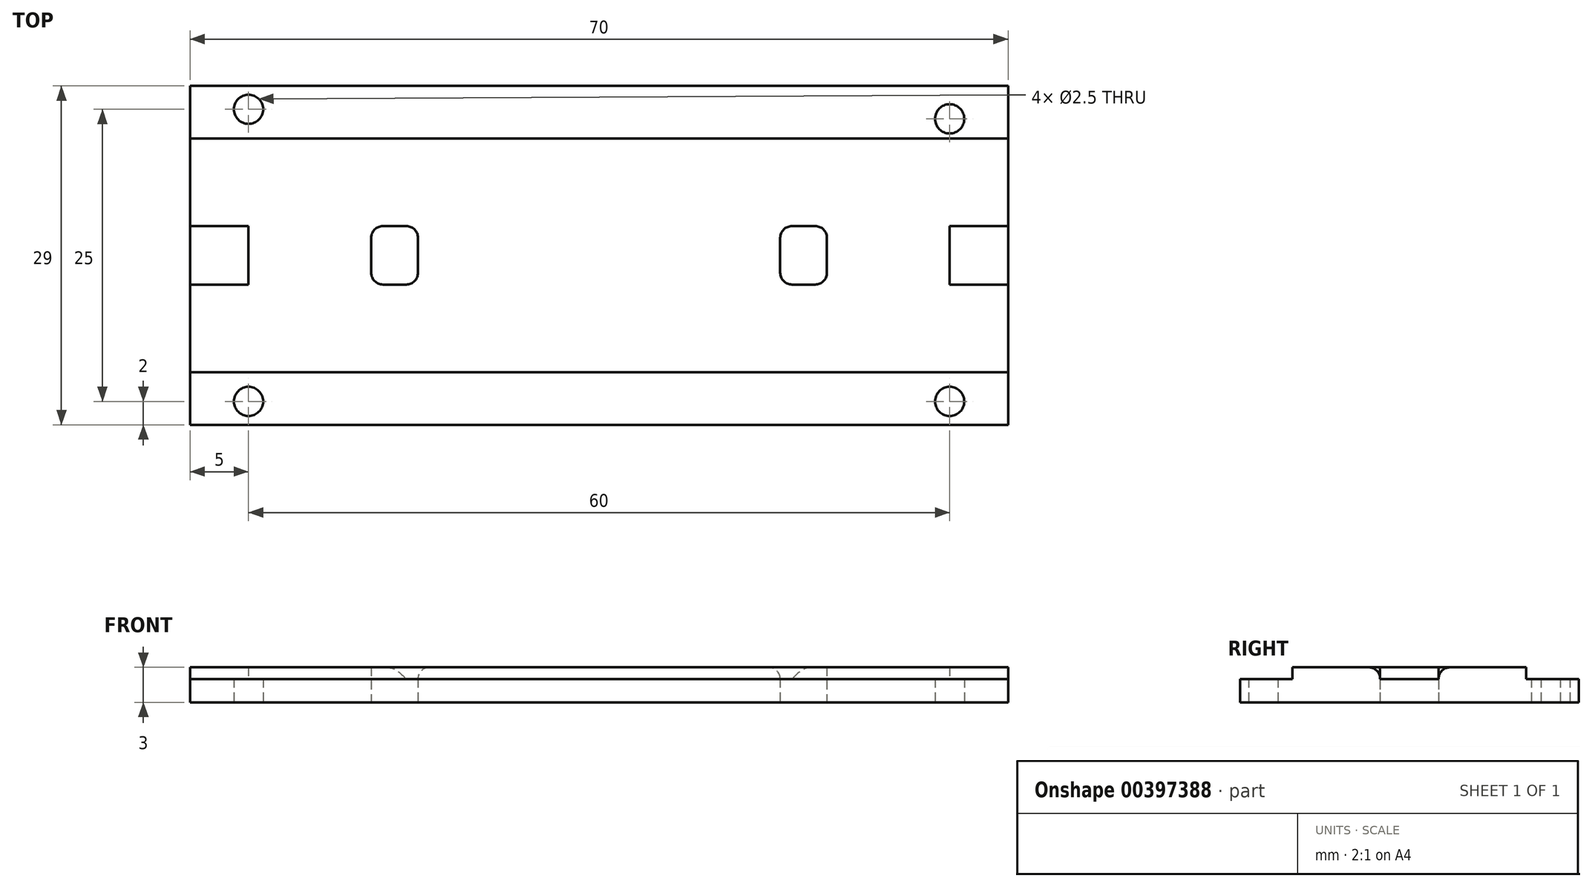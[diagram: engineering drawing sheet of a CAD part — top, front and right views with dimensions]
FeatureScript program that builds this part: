
annotation { "Feature Type Name" : "Feature", "Feature Type Description" : "" }
export const myFeature = defineFeature(function(context is Context, id is Id, definition is map)
    precondition{}
    {
        {
            var Q0;
            Q0=qCreatedBy(makeId("Top.planeOp"),FACE);
            var sketch = newSketch(context, id + "F0", { "sketchPlane" : qUnion([Q0])});
            skLineSegment(sketch, "E0.bottom", {"start": v(35, -14.5) * mm, "end": v(-35, -14.5) * mm});
            skLineSegment(sketch, "E0.top", {"start": v(35, 14.5) * mm, "end": v(-35, 14.5) * mm});
            skLineSegment(sketch, "E0.left", {"start": v(35, -14.5) * mm, "end": v(35, 14.5) * mm});
            skLineSegment(sketch, "E0.right", {"start": v(-35, -14.5) * mm, "end": v(-35, 14.5) * mm});
            skPoint(sketch, "E0.middle", {"position": v(0, 0) * mm});
            skLineSegment(sketch, "E1", {"start": v(-35, 10) * mm, "end": v(35, 10) * mm});
            skLineSegment(sketch, "E2", {"start": v(-35, -10) * mm, "end": v(35, -10) * mm});
            skLineSegment(sketch, "E3.bottom", {"start": v(-35, -2.5) * mm, "end": v(-30, -2.5) * mm});
            skLineSegment(sketch, "E3.top", {"start": v(-35, 2.5) * mm, "end": v(-30, 2.5) * mm});
            skLineSegment(sketch, "E3.left", {"start": v(-35, -2.5) * mm, "end": v(-35, 2.5) * mm});
            skLineSegment(sketch, "E3.right", {"start": v(-30, -2.5) * mm, "end": v(-30, 2.5) * mm});
            skPoint(sketch, "E3.middle", {"position": v(-32.5, 0) * mm});
            skPoint(sketch, "E3.middle.positionSnap0", {"position": v(-35, 0) * mm});
            skPoint(sketch, "E3.centerSnap0", {"position": v(-35, 0) * mm});
            skLineSegment(sketch, "E4.bottom", {"start": v(35, -2.5) * mm, "end": v(30, -2.5) * mm});
            skLineSegment(sketch, "E4.top", {"start": v(35, 2.5) * mm, "end": v(30, 2.5) * mm});
            skLineSegment(sketch, "E4.left", {"start": v(35, -2.5) * mm, "end": v(35, 2.5) * mm});
            skLineSegment(sketch, "E4.right", {"start": v(30, -2.5) * mm, "end": v(30, 2.5) * mm});
            skPoint(sketch, "E4.middle", {"position": v(32.5, 0) * mm});
            skPoint(sketch, "E4.cornerSnap0", {"position": v(-32.5, -2.5) * mm});
            skPoint(sketch, "E5", {"position": v(-30, -12.5) * mm});
            skPoint(sketch, "E6", {"position": v(30, -12.5) * mm});
            skPoint(sketch, "E7", {"position": v(30, 11.68) * mm});
            skPoint(sketch, "E8", {"position": v(-30, 12.5) * mm});
            skLineSegment(sketch, "E9.bottom", {"start": v(-15.5, -2.5) * mm, "end": v(-19.5, -2.5) * mm});
            skLineSegment(sketch, "E9.top", {"start": v(-15.5, 2.5) * mm, "end": v(-19.5, 2.5) * mm});
            skLineSegment(sketch, "E9.left", {"start": v(-15.5, -2.5) * mm, "end": v(-15.5, 2.5) * mm});
            skLineSegment(sketch, "E9.right", {"start": v(-19.5, -2.5) * mm, "end": v(-19.5, 2.5) * mm});
            skPoint(sketch, "E9.middle", {"position": v(-17.5, 0) * mm});
            skLineSegment(sketch, "E10.bottom", {"start": v(19.5, -2.5) * mm, "end": v(15.5, -2.5) * mm});
            skLineSegment(sketch, "E10.top", {"start": v(19.5, 2.5) * mm, "end": v(15.5, 2.5) * mm});
            skLineSegment(sketch, "E10.left", {"start": v(19.5, -2.5) * mm, "end": v(19.5, 2.5) * mm});
            skLineSegment(sketch, "E10.right", {"start": v(15.5, -2.5) * mm, "end": v(15.5, 2.5) * mm});
            skPoint(sketch, "E10.middle", {"position": v(17.5, 0) * mm});
            skSolve(sketch);
        }
        {
            var Q0;
            {var subQ4=sQuery(id+"F0.wireOp",EDGE,"E1");Q0=makeQuery(id+"F0.imprint","IMPRINT",FACE,{"disambiguationData":[TD([[makeQuery(id+"F0.imprint","IMPRINT",EDGE,{"derivedFrom":subQ4}),-1.0]])]});}
            extrude(context, id + "F1", {"entities" : qUnion([Q0]), "depth" : 3 * mm});
        }
        {
            var Q0;
            Q0=makeQuery(id+"F0.imprint","IMPRINT",FACE,{"disambiguationData":[TD([[makeQuery(id+"F0.imprint","IMPRINT",EDGE,{"derivedFrom":sQuery(id+"F0.wireOp",EDGE,"E3.bottom")}),1.0]])]});
            var Q1;
            {var subQ0=sQuery(id+"F0.wireOp",EDGE,"E0.top");Q1=makeQuery(id+"F0.imprint","IMPRINT",FACE,{"disambiguationData":[TD([[makeQuery(id+"F0.imprint","IMPRINT",EDGE,{"derivedFrom":subQ0}),1.0]])]});}
            var Q2;
            {var subQ0=sQuery(id+"F0.wireOp",EDGE,"E0.bottom");Q2=makeQuery(id+"F0.imprint","IMPRINT",FACE,{"disambiguationData":[TD([[makeQuery(id+"F0.imprint","IMPRINT",EDGE,{"derivedFrom":subQ0}),-1.0]])]});}
            var Q3;
            Q3=makeQuery(id+"F0.imprint","IMPRINT",FACE,{"disambiguationData":[TD([[makeQuery(id+"F0.imprint","IMPRINT",EDGE,{"derivedFrom":sQuery(id+"F0.wireOp",EDGE,"E4.bottom")}),-1.0]])]});
            extrude(context, id + "F2", {"entities" : qUnion([Q0, Q1, Q2, Q3]), "operationType" : NewBodyOperationType.ADD, "depth" : 2 * mm});
        }
        {
            var Q0;
            Q0=sQuery(id+"F0.wireOp",VERTEX,"E5");
            var Q1;
            Q1=sQuery(id+"F0.wireOp",VERTEX,"E8");
            var Q2;
            Q2=sQuery(id+"F0.wireOp",VERTEX,"E7");
            var Q3;
            Q3=sQuery(id+"F0.wireOp",VERTEX,"E6");
            var Q4;
            Q4=makeQuery(id+"F1.opExtrude","SWEPT_BODY",BODY,{"disambiguationData":[OSD([sQuery(id+"F0.wireOp",EDGE,"E0.left"),sQuery(id+"F0.wireOp",EDGE,"E0.right"),sQuery(id+"F0.wireOp",EDGE,"E1"),sQuery(id+"F0.wireOp",EDGE,"E2"),sQuery(id+"F0.wireOp",EDGE,"E3.bottom"),sQuery(id+"F0.wireOp",EDGE,"E3.top"),sQuery(id+"F0.wireOp",EDGE,"E3.right"),sQuery(id+"F0.wireOp",EDGE,"E4.bottom"),sQuery(id+"F0.wireOp",EDGE,"E4.top"),sQuery(id+"F0.wireOp",EDGE,"E4.right")])]});
            hole(context, id + "F3", {"style" : HoleStyle.SIMPLE, "endStyle" : HoleEndStyle.THROUGH, "oppositeDirection" : true, "holeDiameter" : 2.5 * mm, "isTappedThrough" : true, "tappedDepth" : 12 * mm, "tapClearance" : 3, "locations" : qUnion([Q0, Q1, Q2, Q3]), "scope" : qUnion([Q4])});
        }
        {
            var Q0;
            Q0=makeQuery(id+"F1.opExtrude","SWEPT_EDGE",EDGE,{"disambiguationData":[OSD([sQuery(id+"F0.wireOp",EDGE,"E9.top"),sQuery(id+"F0.wireOp",EDGE,"E9.right")])]});
            var Q1;
            Q1=makeQuery(id+"F1.opExtrude","SWEPT_EDGE",EDGE,{"disambiguationData":[OSD([sQuery(id+"F0.wireOp",EDGE,"E9.top"),sQuery(id+"F0.wireOp",EDGE,"E9.left")])]});
            var Q2;
            Q2=makeQuery(id+"F1.opExtrude","SWEPT_EDGE",EDGE,{"disambiguationData":[OSD([sQuery(id+"F0.wireOp",EDGE,"E9.bottom"),sQuery(id+"F0.wireOp",EDGE,"E9.left")])]});
            var Q3;
            Q3=makeQuery(id+"F1.opExtrude","SWEPT_EDGE",EDGE,{"disambiguationData":[OSD([sQuery(id+"F0.wireOp",EDGE,"E9.bottom"),sQuery(id+"F0.wireOp",EDGE,"E9.right")])]});
            var Q4;
            Q4=makeQuery(id+"F1.opExtrude","SWEPT_EDGE",EDGE,{"disambiguationData":[OSD([sQuery(id+"F0.wireOp",EDGE,"E10.top"),sQuery(id+"F0.wireOp",EDGE,"E10.left")])]});
            var Q5;
            Q5=makeQuery(id+"F1.opExtrude","SWEPT_EDGE",EDGE,{"disambiguationData":[OSD([sQuery(id+"F0.wireOp",EDGE,"E10.bottom"),sQuery(id+"F0.wireOp",EDGE,"E10.left")])]});
            var Q6;
            Q6=makeQuery(id+"F1.opExtrude","SWEPT_EDGE",EDGE,{"disambiguationData":[OSD([sQuery(id+"F0.wireOp",EDGE,"E10.bottom"),sQuery(id+"F0.wireOp",EDGE,"E10.right")])]});
            var Q7;
            Q7=makeQuery(id+"F1.opExtrude","SWEPT_EDGE",EDGE,{"disambiguationData":[OSD([sQuery(id+"F0.wireOp",EDGE,"E10.top"),sQuery(id+"F0.wireOp",EDGE,"E10.right")])]});
            var Q8;
            Q8=makeQuery(id+"F1.opExtrude","CAP_EDGE",EDGE,{"disambiguationData":[OSD([sQuery(id+"F0.wireOp",EDGE,"E10.right")])],"isStart":false});
            var Q9;
            Q9=makeQuery(id+"F1.opExtrude","CAP_EDGE",EDGE,{"disambiguationData":[OSD([sQuery(id+"F0.wireOp",EDGE,"E9.left")])],"isStart":false});
            fillet(context, id + "F4", {"entities" : qUnion([Q0, Q1, Q2, Q3, Q4, Q5, Q6, Q7, Q8, Q9]), "radius" : 1 * mm, "tangentPropagation" : true, "allowEdgeOverflow" : false});
        }
    });
